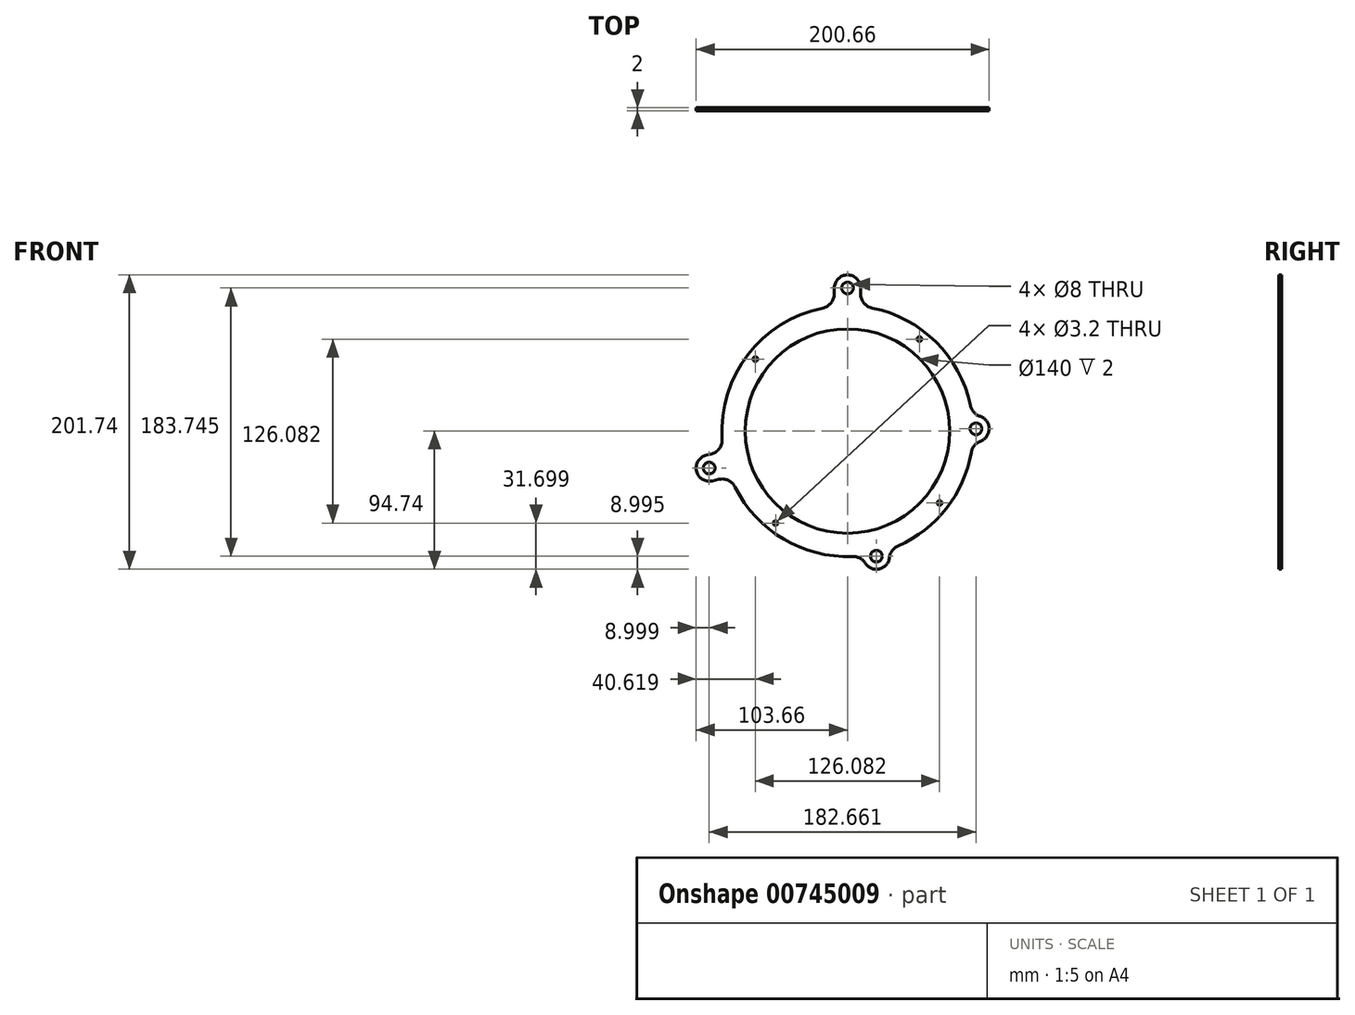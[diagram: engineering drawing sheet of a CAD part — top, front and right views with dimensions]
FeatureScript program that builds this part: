
annotation { "Feature Type Name" : "Feature", "Feature Type Description" : "" }
export const myFeature = defineFeature(function(context is Context, id is Id, definition is map)
    precondition{}
    {
        {
            var Q0;
            Q0=qCreatedBy(makeId("Front.planeOp"),FACE);
            var sketch = newSketch(context, id + "F0", { "sketchPlane" : qUnion([Q0])});
            skArc(sketch, "E0", {"start": v(-17.02, 84.3) * mm, "mid": v(-68.26, 52.3) * mm, "end": v(-85.82, -5.5) * mm});
            skCircle(sketch, "E1", {"center": v(0, 0) * mm, "radius": 70 * mm});
            skCircle(sketch, "E2", {"center": v(0, 98) * mm, "radius": 4 * mm});
            skArc(sketch, "E3", {"start": v(9, 98) * mm, "mid": v(0, 107) * mm, "end": v(-9, 98) * mm});
            skLineSegment(sketch, "E4", {"start": v(0, 128.16) * mm, "end": v(0, -110.65) * mm, "construction": true});
            skLineSegment(sketch, "E5", {"start": v(-104.33, 0) * mm, "end": v(119.2, 0) * mm, "construction": true});
            skLineSegment(sketch, "E6", {"start": v(-9, 98) * mm, "end": v(-9, 94.1) * mm});
            skLineSegment(sketch, "E7", {"start": v(9, 98) * mm, "end": v(9, 94.1) * mm});
            skLineSegment(sketch, "E8", {"start": v(-26.03, 98) * mm, "end": v(34.99, 98) * mm, "construction": true});
            skLineSegment(sketch, "E9", {"start": v(0, 0) * mm, "end": v(109.54, 1.91) * mm, "construction": true});
            skCircle(sketch, "E10", {"center": v(88, 1.54) * mm, "radius": 4 * mm});
            skLineSegment(sketch, "E11", {"start": v(0, 0) * mm, "end": v(-99.51, -26.66) * mm, "construction": true});
            skCircle(sketch, "E12", {"center": v(-94.66, -25.36) * mm, "radius": 4 * mm});
            skLineSegment(sketch, "E13", {"start": v(0, 0) * mm, "end": v(23.05, -99.86) * mm, "construction": true});
            skCircle(sketch, "E14", {"center": v(19.8, -85.74) * mm, "radius": 4 * mm});
            skArc(sketch, "E15", {"start": v(-96.69, -16.6) * mm, "mid": v(-103.43, -27.39) * mm, "end": v(-92.64, -34.13) * mm});
            skLineSegment(sketch, "E16", {"start": v(-96.69, -16.6) * mm, "end": v(-93.55, -15.87) * mm});
            skLineSegment(sketch, "E17", {"start": v(-92.64, -34.13) * mm, "end": v(-88.16, -33.1) * mm});
            skArc(sketch, "E18.trimOffspring", {"start": v(-76.96, -38.38) * mm, "mid": v(-43.81, -74) * mm, "end": v(3.36, -85.93) * mm});
            skArc(sketch, "E19", {"start": v(12.2, -90.57) * mm, "mid": v(21.82, -94.51) * mm, "end": v(28.74, -86.75) * mm});
            skArc(sketch, "E20.trimOffspring", {"start": v(34.65, -78.71) * mm, "mid": v(67.77, -52.95) * mm, "end": v(84.75, -14.58) * mm});
            skArc(sketch, "E21", {"start": v(91.13, -6.9) * mm, "mid": v(97, 1.7) * mm, "end": v(90.83, 10.08) * mm});
            skArc(sketch, "E22.trimOffspring", {"start": v(84.2, 17.53) * mm, "mid": v(60.63, 61) * mm, "end": v(17.02, 84.3) * mm});
            skPoint(sketch, "E23.visualSharp", {"position": v(-9, 85.53) * mm});
            skArc(sketch, "E23.filletArc", {"start": v(-17.02, 84.3) * mm, "mid": v(-11.26, 87.77) * mm, "end": v(-9, 94.1) * mm});
            skPoint(sketch, "E24.visualSharp", {"position": v(9, 85.53) * mm});
            skArc(sketch, "E24.filletArc", {"start": v(9, 94.1) * mm, "mid": v(11.26, 87.77) * mm, "end": v(17.02, 84.3) * mm});
            skPoint(sketch, "E25.visualSharp", {"position": v(-84.87, -13.87) * mm});
            skArc(sketch, "E25.filletArc", {"start": v(-93.55, -15.87) * mm, "mid": v(-87.78, -12.1) * mm, "end": v(-85.82, -5.5) * mm});
            skPoint(sketch, "E26.visualSharp", {"position": v(-80.12, -31.24) * mm});
            skArc(sketch, "E26.filletArc", {"start": v(-76.96, -38.38) * mm, "mid": v(-81.64, -33.8) * mm, "end": v(-88.16, -33.1) * mm});
            skPoint(sketch, "E27.visualSharp", {"position": v(85.4, 10.15) * mm});
            skArc(sketch, "E27.filletArc", {"start": v(84.2, 17.53) * mm, "mid": v(86.52, 12.92) * mm, "end": v(90.83, 10.08) * mm});
            skPoint(sketch, "E28.visualSharp", {"position": v(85.7, -7.17) * mm});
            skArc(sketch, "E28.filletArc", {"start": v(91.13, -6.9) * mm, "mid": v(86.92, -9.89) * mm, "end": v(84.75, -14.58) * mm});
            skPoint(sketch, "E29.visualSharp", {"position": v(27.69, -81.42) * mm});
            skArc(sketch, "E29.filletArc", {"start": v(34.65, -78.71) * mm, "mid": v(30.62, -81.94) * mm, "end": v(28.74, -86.75) * mm});
            skPoint(sketch, "E30.visualSharp", {"position": v(10.8, -85.32) * mm});
            skArc(sketch, "E30.filletArc", {"start": v(12.2, -90.57) * mm, "mid": v(8.4, -87.07) * mm, "end": v(3.36, -85.93) * mm});
            skLineSegment(sketch, "E31", {"start": v(-97.82, -11.67) * mm, "end": v(-91.35, -39.7) * mm, "construction": true});
            skCircle(sketch, "E32", {"center": v(0, 0) * mm, "radius": 80 * mm, "construction": true});
            skLineSegment(sketch, "E33", {"start": v(0, 0) * mm, "end": v(84.11, -65.72) * mm, "construction": true});
            skCircle(sketch, "E34", {"center": v(63.04, -49.25) * mm, "radius": 1.6 * mm});
            skLineSegment(sketch, "E35", {"start": v(0, 0) * mm, "end": v(-65.97, -84.44) * mm, "construction": true});
            skLineSegment(sketch, "E36", {"start": v(0, 0) * mm, "end": v(-96.75, 75.59) * mm, "construction": true});
            skCircle(sketch, "E37", {"center": v(-63.04, 49.25) * mm, "radius": 1.6 * mm});
            skLineSegment(sketch, "E38", {"start": v(0, 0) * mm, "end": v(65.2, 83.45) * mm, "construction": true});
            skCircle(sketch, "E39", {"center": v(49.25, 63.04) * mm, "radius": 1.6 * mm});
            skCircle(sketch, "E40", {"center": v(-49.25, -63.04) * mm, "radius": 1.6 * mm});
            skSolve(sketch);
        }
        {
            var Q0;
            Q0 = qSketchRegion(id + "F0", true);
            extrude(context, id + "F1", {"entities" : qUnion([Q0]), "depth" : 2 * mm, "offsetDistance" : 25 * mm});
        }
    });
